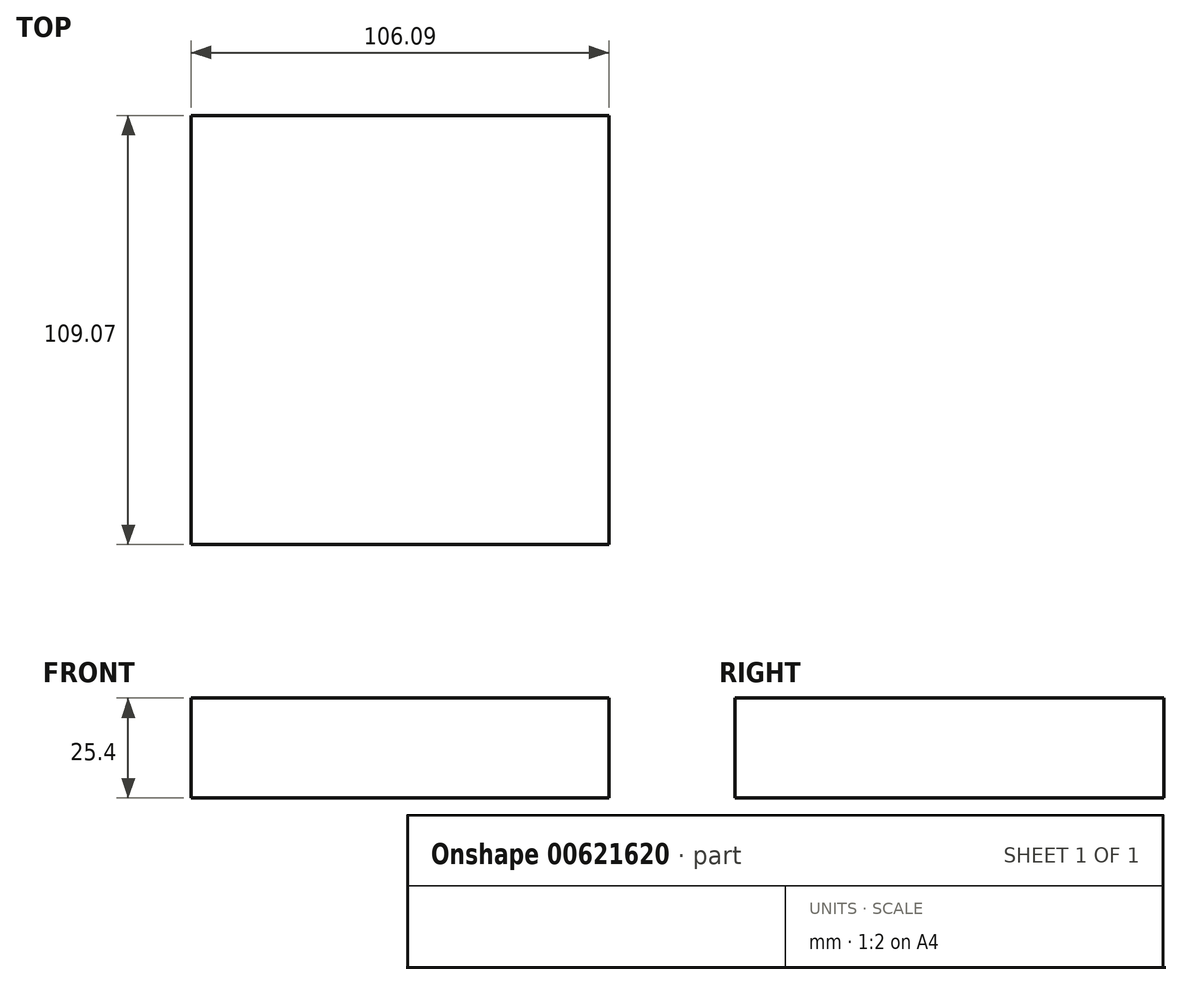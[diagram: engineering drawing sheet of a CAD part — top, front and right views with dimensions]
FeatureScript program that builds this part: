
annotation { "Feature Type Name" : "Feature", "Feature Type Description" : "" }
export const myFeature = defineFeature(function(context is Context, id is Id, definition is map)
    precondition{}
    {
        {
            var Q0;
            Q0=qCreatedBy(makeId("Top.planeOp"),FACE);
            var sketch = newSketch(context, id + "F0", { "sketchPlane" : qUnion([Q0])});
            skLineSegment(sketch, "E0.bottom", {"start": v(0, 0) * mm, "end": v(106.09, 0) * mm});
            skLineSegment(sketch, "E0.top", {"start": v(0, 109.07) * mm, "end": v(106.09, 109.07) * mm});
            skLineSegment(sketch, "E0.left", {"start": v(0, 0) * mm, "end": v(0, 109.07) * mm});
            skLineSegment(sketch, "E0.right", {"start": v(106.09, 0) * mm, "end": v(106.09, 109.07) * mm});
            skSolve(sketch);
        }
        {
            var Q0;
            Q0 = qSketchRegion(id + "F0", true);
            extrude(context, id + "F1", {"entities" : qUnion([Q0]), "depth" : 25.4 * mm, "offsetDistance" : 25.4 * mm});
        }
    });
